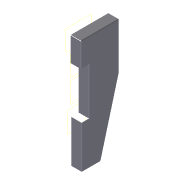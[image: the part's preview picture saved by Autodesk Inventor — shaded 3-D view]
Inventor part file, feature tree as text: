
AUTODESK INVENTOR PART (.ipt)
format: ipt  version: 2015 (Build 190159000, 159)  size: 190,464 bytes
history: native  units: mm
features: reference x8, sheet_metal_op x4, sketch x3, other x2, mirror x1
ambient origin geometry x8: Origin, YZ Plane, XZ Plane, XY Plane, X Axis, Y Axis, Z Axis, Center Point
bodies: Solid1 (feature_tree)
feature tree (18):
  sheet_metal_op  "Face1"
  sketch  "Sketch3"  dims[d16=445.0mm]
  sheet_metal_op  "Flange4"
  mirror  "Mirror1"
  sketch  "Sketch1"  dims[d1=1.6mm]
  reference  "Reference1"
  reference  "Reference2"
  other  "Plate1"
  reference  "Reference3"
  reference  "Reference4"
  reference  "Reference5"
  reference  "Reference6"
  reference  "Reference7"
  reference  "Reference8"
  sketch  "Sketch6"  dims[d17=35.0mm d18=50.0mm d19=3.922832mm d40=5.0mm d41=48.571429mm d42=5.0mm d43=5.0mm d44=1.6mm d45=0.8mm d46=3.2mm d47=1.6mm d48=40.0mm d49=90.0deg d50=1.6mm d51=6.4mm d52=1.6mm d53=1.6mm d54=150.0mm d55=75.0mm]
  other  "Plate5"
  sheet_metal_op  "Bend4"
  sheet_metal_op  "Corner4"
